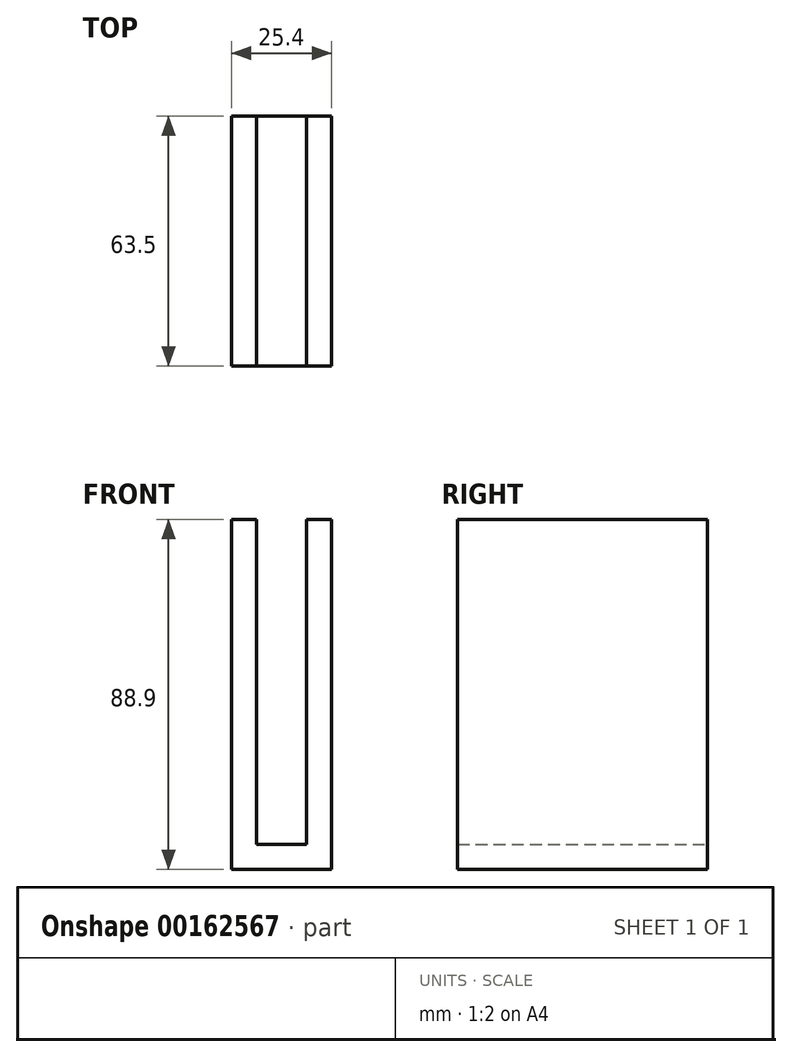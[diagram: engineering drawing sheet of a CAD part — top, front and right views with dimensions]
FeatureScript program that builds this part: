
annotation { "Feature Type Name" : "Feature", "Feature Type Description" : "" }
export const myFeature = defineFeature(function(context is Context, id is Id, definition is map)
    precondition{}
    {
        {
            var Q0;
            Q0=qCreatedBy(makeId("Front.planeOp"),FACE);
            var sketch = newSketch(context, id + "F0", { "sketchPlane" : qUnion([Q0])});
            skLineSegment(sketch, "E0", {"start": v(-41.04, 46.97) * mm, "end": v(-34.69, 46.97) * mm});
            skLineSegment(sketch, "E1", {"start": v(-34.69, 46.97) * mm, "end": v(-34.69, -35.58) * mm});
            skLineSegment(sketch, "E2", {"start": v(-34.69, -35.58) * mm, "end": v(-21.99, -35.58) * mm});
            skLineSegment(sketch, "E3", {"start": v(-21.99, -35.58) * mm, "end": v(-21.99, 46.97) * mm});
            skLineSegment(sketch, "E4", {"start": v(-21.99, 46.97) * mm, "end": v(-15.64, 46.97) * mm});
            skLineSegment(sketch, "E5", {"start": v(-15.64, 46.97) * mm, "end": v(-15.64, -41.93) * mm});
            skLineSegment(sketch, "E6", {"start": v(-15.64, -41.93) * mm, "end": v(-41.04, -41.93) * mm});
            skLineSegment(sketch, "E7", {"start": v(-41.04, -41.93) * mm, "end": v(-41.04, 46.97) * mm});
            skSolve(sketch);
        }
        {
            var Q0;
            Q0 = qSketchRegion(id + "F0", true);
            extrude(context, id + "F1", {"entities" : qUnion([Q0]), "depth" : 63.5 * mm});
        }
    });
